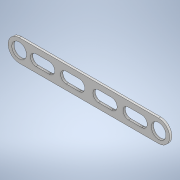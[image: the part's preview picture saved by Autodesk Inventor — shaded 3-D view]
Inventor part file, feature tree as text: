
AUTODESK INVENTOR PART (.ipt)
format: ipt  version: 2022 (Build 260153000, 153)  size: 161,792 bytes
history: native  units: mm
features: extrude x1, sketch x1
ambient origin geometry x8: Origin, YZ Plane, XZ Plane, XY Plane, X Axis, Y Axis, Z Axis, Center Point
bodies: Body1 (feature_tree)
feature tree (2):
  extrude  "Extrusion2"  Depth=30.0mm
  sketch  "Sketch2"  dims[d27=190.0mm d28=30.0mm d29=20.0mm d30=20.0mm d31=18.0mm d32=15.0mm d41=20.0mm d43=41.0mm d44=10.0mm d46=10.0mm d48=41.0mm d49=3.0mm d50=0.0mm]
